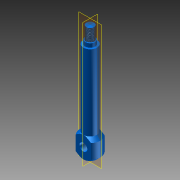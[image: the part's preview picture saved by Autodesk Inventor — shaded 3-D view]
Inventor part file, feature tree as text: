
AUTODESK INVENTOR PART (.ipt)
format: ipt  version: 2011 (Build 150229000, 229)  size: 130,048 bytes
history: native  units: mm (DEFAULTED — no unit token found)
features: sketch x2, revolve x1, hole x1, mirror x1, chamfer x1
ambient origin geometry x8: Origin, YZ Plane, XZ Plane, XY Plane, X Axis, Y Axis, Z Axis, Center Point
feature tree (6):
  revolve  "Revolution1"  [1 undecoded]
  sketch  "Sketch2"  dims[d10=21.0mm d11=14.0mm d12=22.0mm d13=100.0mm d14=104.0mm d15=117.0mm d16=8.0mm d17=10.0mm d18=3.5mm d19=2.0mm d20=45.0deg d21=10.0mm d22=0.0mm d23=10.0mm d24=0.0mm d25=8.0mm d26=6.0mm d27=4.0mm d28=2.0mm d29=90.0deg d30=8.0mm d31=20.594885mm]
  hole  "Hole1"  [1 undecoded]
  mirror  "Mirror1"
  chamfer  "Chamfer1"  Distance=22.0mm
  sketch  "Sketch1"  dims[d0=90.0deg d1=8.0mm]
note: 2 required parameter values undecoded (feature->parameter linkage not recoverable at this tier; creation-order binding heuristic only, values carry confidence <= 0.55)